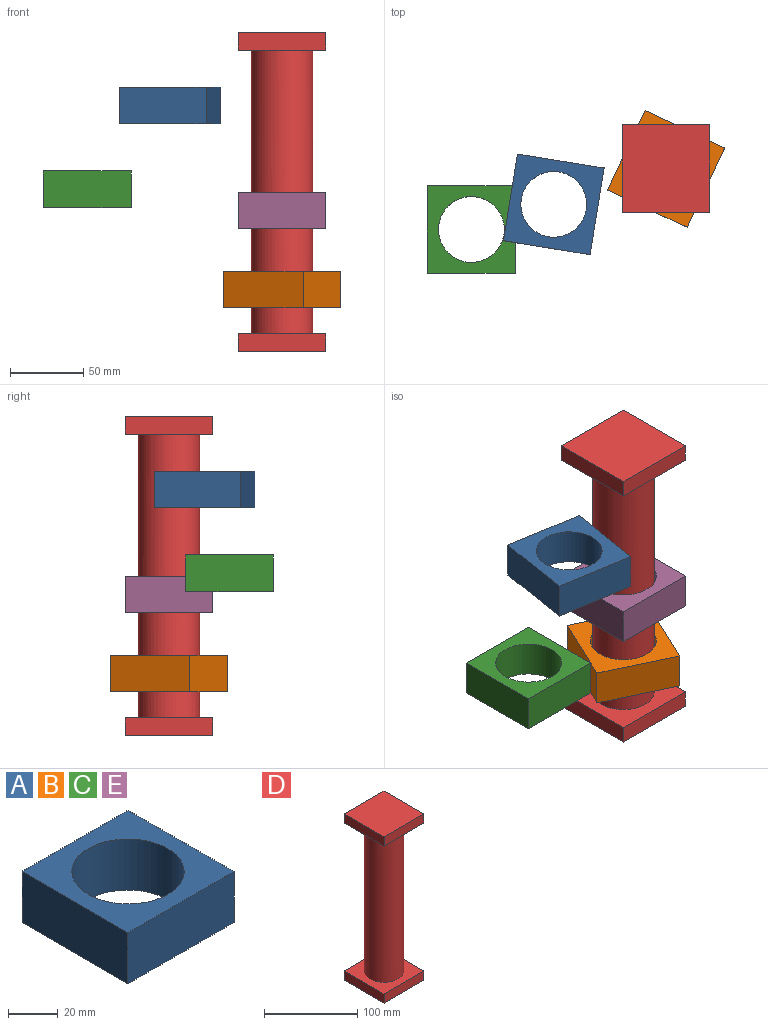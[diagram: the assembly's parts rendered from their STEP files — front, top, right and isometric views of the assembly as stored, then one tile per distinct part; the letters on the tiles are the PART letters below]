
ASSEMBLY  parts=5 mates=2
PART A: 7 faces, bbox 60x60x25 mm
  f0: plane 60x25mm, normal (-1,0,0), area 1500mm2, adj f1,f3,f4,f5
  f1: plane 60x25mm, normal (0,-1,0), area 1500mm2, adj f0,f2,f4,f5
  f2: plane 60x25mm, normal (1,0,0), area 1500mm2, adj f1,f3,f4,f5
  f3: plane 60x25mm, normal (0,1,0), area 1500mm2, adj f0,f2,f4,f5
  f4: plane 60x60mm, normal (0,0,1), area 2009.6mm2, adj f0,f1,f2,f3,f6
  f5: plane 60x60mm, normal (0,0,-1), area 2009.6mm2, adj f0,f1,f2,f3,f6
  f6: cylinder r=22.5mm len=45mm, axis (0,0,1), area 3534.3mm2, adj f4,f5
PART B: same geometry as A
PART C: same geometry as A
PART D: 13 faces, bbox 60x60x218 mm
  f0: cylinder r=21mm len=194mm, axis (0,0,-1), area 25597.7mm2, adj f6,f12
  f1: plane 60x12mm, normal (1,0,0), area 720mm2, adj f2,f4,f5,f6
  f2: plane 60x12mm, normal (0,-1,0), area 720mm2, adj f1,f3,f5,f6
  f3: plane 60x12mm, normal (-1,0,0), area 720mm2, adj f2,f4,f5,f6
  f4: plane 60x12mm, normal (0,1,0), area 720mm2, adj f1,f3,f5,f6
  f5: plane 60x60mm, normal (0,0,-1), area 3600mm2, adj f1,f2,f3,f4
  f6: plane 60x60mm, normal (0,0,1), area 2214.6mm2, adj f0,f1,f2,f3,f4
  f7: plane 60x12mm, normal (-1,0,0), area 720mm2, adj f8,f10,f11,f12
  f8: plane 60x12mm, normal (0,-1,0), area 720mm2, adj f7,f9,f11,f12
  f9: plane 60x12mm, normal (1,0,0), area 720mm2, adj f8,f10,f11,f12
  f10: plane 60x12mm, normal (0,1,0), area 720mm2, adj f7,f9,f11,f12
  f11: plane 60x60mm, normal (0,0,1), area 3600mm2, adj f7,f8,f9,f10
  f12: plane 60x60mm, normal (0,0,-1), area 2214.6mm2, adj f0,f7,f8,f9,f10
PART E: same geometry as A
PLACE A rot(axis=(0,0,-1),99.2deg) t=(-134.66,-12.63,41.12)mm
PLACE B rot(axis=(0,0,1),154.8deg) t=(-57.84,11.76,-84.71)mm
PLACE C t=(-190.97,-29.73,-16.14)mm
PLACE D t=(-57.84,11.76,-8.53)mm fixed
PLACE E t=(-57.84,11.76,-30.53)mm
MATE cylindrical B.f6 <-> D.f0  axis (0,0,1) through (-57.84,11.76,-59.71)mm
MATE cylindrical E.f6 <-> D.f0  axis (0,0,1) through (-57.84,11.76,-5.53)mm
